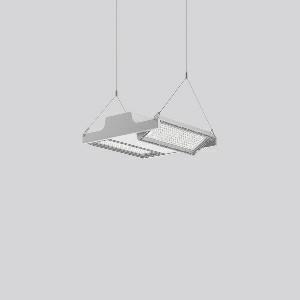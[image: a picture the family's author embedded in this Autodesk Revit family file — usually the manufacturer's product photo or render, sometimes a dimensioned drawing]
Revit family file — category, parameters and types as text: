
# Revit family: light_case_921682_004_76_6553
name_source: partatom
category: Lighting Fixtures
units: mm (PartAtom-declared; Revit-internal decimal feet)

## family parameters
Cut with Voids When Loaded = No
Host = Face
Light Source = No
Part Type = Normal
Room Calculation Point = No
Round Connector Dimension = Use Diameter
Shared = No

## types (1)
- LIGHT CASE (1 x LED Modul 840, 8900 lm, 4000)
    Apparent Load = 117 VA
    CIE Flux Codes = 81 98 100 100 100
    Color Rendering = 80
    Color Temperature = 4000
    Default Elevation = 1800 mm
    Description = Series: LIGHT CASE
Flat highbay luminaire for chain or cable suspension with 2 LED modules that can be swivelled. Housing: die cast aluminium and sheet steel, powder-coated. Optimised thermal management thanks to special luminaire design. Self-cleaning heat sink for constant heat dissipation. Cover: plastic (polycarbonate, shockproof), with integrated four-row lens system. LED modules can be swivelled ± 30° for optimum illumination. Suitable for chain or steel cable suspension (to be provided on site). With 5-pin connection terminal (1.5 m). With integrated movement sensor and light sensor for daylight detection on request. Ball impact proof in accordance with DIN 18032-03 (except steel cable suspension). Luminaire with limited surface temperature in accordance with EN 60598-2-24 for use in environments in which a deposit of conductive dust on the luminaire can be expected. 
Colour: silver, matt (approx. RAL 9006)
Length: 406 mm
Width: 397 mm
Height: 110 mm
Lamp: LED
Socket: without socket
Colour temperature: 4000K
Colour rendering index (CRI): 80
System power: 117 W
Rated luminous flux: 17800 lm
Luminous efficiency: 152 lm/W
Control gear: Converter, dimmable, DALI
Protection class: I
Type of protection: IP 65
    Height = 110 mm
    Lamp = 1 x LED Modul 840
    Lamp Light Flux = 8900 lm
    Lamp count = 1
    Length = 406 mm
    Lifetime = 50000 h
    Luminous efficacy = 152 lm/W
    Manufacturer = RZB
    ModVariant = No
    Model = 921682.004.76
    Mounting Place = Ceiling
    Mounting Type = Pendant
    Number of Poles = 1
    OnlyDefault = Yes
    Power Factor = 1
    Product Name = LIGHT CASE
    Product group = Pendant commercial luminaires
    ProductGroupID = 903
    Protection Class = Protection class I
    Protection Degree = IP 65
    RLX_Detail_Level = 1
    RLX_Emergency_Light_Flux = 0 lm
    RLX_Emergency_Type = 0
    RLX_Emergency_Type_DB = No
    RlxData = <blob elided: 24813 chars, md5=b65fc14f>
    Socket = socket
    Standby Power = 0 W
    System Light Flux = 17800 lm
    System Power = 117 W
    Type Comments = Product without accessories
    Type Image = 921517.004.76.jpg
    URL = http://relux.com
    VarID = ---
    Voltage = 230 V
    Voltage Range = 220-240 V
    Weight = 0.00 kg
    Width = 397 mm

## geometry (parser evidence)
native form markers: Blend x4, Sweep x16
no freeform markers — native parametric forms only
